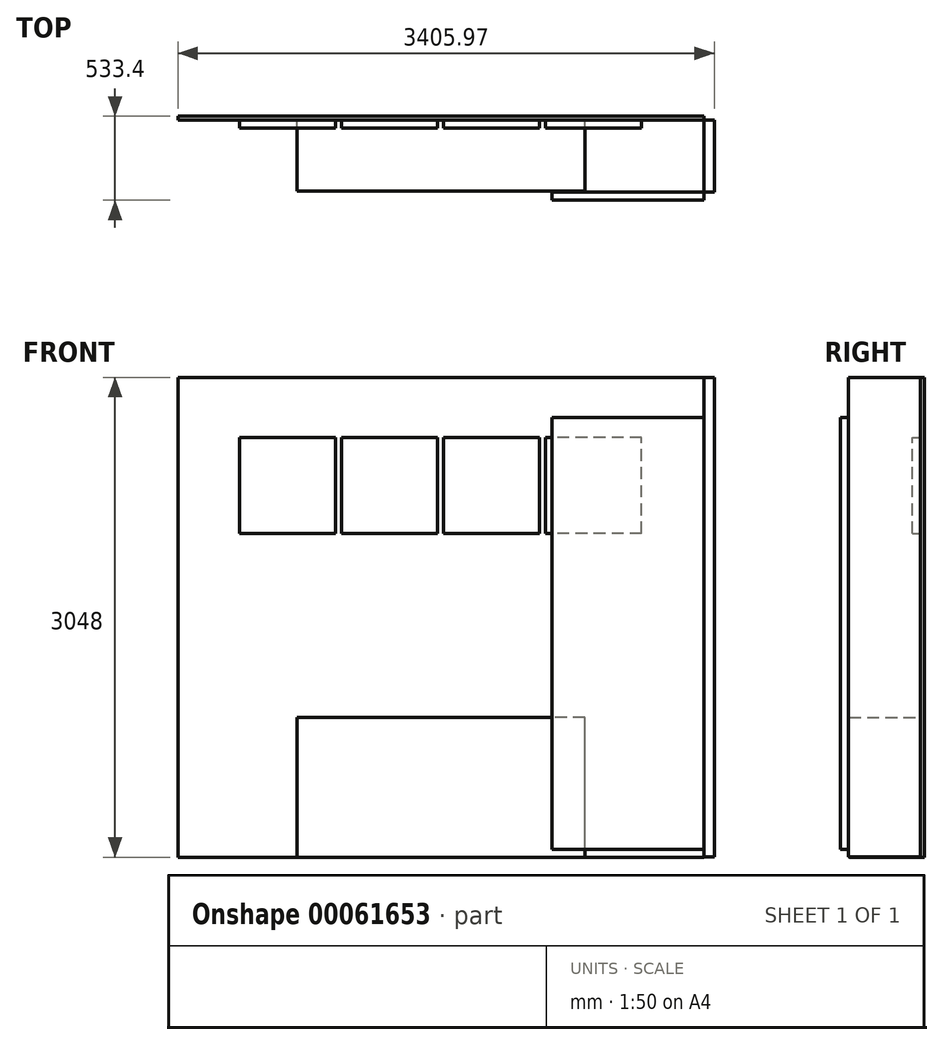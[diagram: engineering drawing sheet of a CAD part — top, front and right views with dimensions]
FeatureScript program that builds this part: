
annotation { "Feature Type Name" : "Feature", "Feature Type Description" : "" }
export const myFeature = defineFeature(function(context is Context, id is Id, definition is map)
    precondition{}
    {
        {
            var Q0;
            Q0=qCreatedBy(makeId("Front.planeOp"),FACE);
            var sketch = newSketch(context, id + "F0", { "sketchPlane" : qUnion([Q0])});
            skLineSegment(sketch, "E0.rect.bottom", {"start": v(1670.05, -1524) * mm, "end": v(-1670.05, -1524) * mm});
            skLineSegment(sketch, "E0.rect.top", {"start": v(1670.05, 1524) * mm, "end": v(-1670.05, 1524) * mm});
            skLineSegment(sketch, "E0.rect.left", {"start": v(1670.05, -1524) * mm, "end": v(1670.05, 1524) * mm});
            skLineSegment(sketch, "E0.rect.right", {"start": v(-1670.05, -1524) * mm, "end": v(-1670.05, 1524) * mm});
            skPoint(sketch, "E0.rect.middle", {"position": v(0, 0) * mm});
            skSolve(sketch);
        }
        {
            var Q0;
            Q0=makeQuery(id+"F0.imprint","IMPRINT",FACE,{"disambiguationData":[TD([[makeQuery(id+"F0.imprint","IMPRINT",EDGE,{"derivedFrom":sQuery(id+"F0.wireOp",EDGE,"E0.rect.bottom")}),-1.0]])]});
            extrude(context, id + "F1", {"entities" : qUnion([Q0]), "depth" : 25.4 * mm});
        }
        {
            var Q0;
            Q0=makeQuery(id+"F1.opExtrude","CAP_FACE",FACE,{"disambiguationData":[OSD([sQuery(id+"F0.wireOp",EDGE,"E0.rect.bottom"),sQuery(id+"F0.wireOp",EDGE,"E0.rect.top"),sQuery(id+"F0.wireOp",EDGE,"E0.rect.left"),sQuery(id+"F0.wireOp",EDGE,"E0.rect.right")])],"isStart":false});
            var sketch = newSketch(context, id + "F2", { "sketchPlane" : qUnion([Q0])});
            skLineSegment(sketch, "E1.rect.bottom", {"start": v(-668.38, 533.23) * mm, "end": v(-1277.98, 533.23) * mm});
            skLineSegment(sketch, "E1.rect.top", {"start": v(-668.38, 1142.83) * mm, "end": v(-1277.98, 1142.83) * mm});
            skLineSegment(sketch, "E1.rect.left", {"start": v(-668.38, 533.23) * mm, "end": v(-668.38, 1142.83) * mm});
            skLineSegment(sketch, "E1.rect.right", {"start": v(-1277.98, 533.23) * mm, "end": v(-1277.98, 1142.83) * mm});
            skPoint(sketch, "E1.rect.middle", {"position": v(-973.18, 838.03) * mm});
            skLineSegment(sketch, "E2.1.0.0", {"start": v(-20.68, 1142.83) * mm, "end": v(-630.28, 1142.83) * mm});
            skLineSegment(sketch, "E2.1.0.1", {"start": v(-20.68, 533.23) * mm, "end": v(-20.68, 1142.83) * mm});
            skLineSegment(sketch, "E2.1.0.2", {"start": v(-20.68, 533.23) * mm, "end": v(-630.28, 533.23) * mm});
            skLineSegment(sketch, "E2.1.0.3", {"start": v(-630.28, 533.23) * mm, "end": v(-630.28, 1142.83) * mm});
            skLineSegment(sketch, "E2.2.0.0", {"start": v(627.02, 1142.83) * mm, "end": v(17.42, 1142.83) * mm});
            skLineSegment(sketch, "E2.2.0.1", {"start": v(627.02, 533.23) * mm, "end": v(627.02, 1142.83) * mm});
            skLineSegment(sketch, "E2.2.0.2", {"start": v(627.02, 533.23) * mm, "end": v(17.42, 533.23) * mm});
            skLineSegment(sketch, "E2.2.0.3", {"start": v(17.42, 533.23) * mm, "end": v(17.42, 1142.83) * mm});
            skLineSegment(sketch, "E2.3.0.0", {"start": v(1274.72, 1142.83) * mm, "end": v(665.12, 1142.83) * mm});
            skLineSegment(sketch, "E2.3.0.1", {"start": v(1274.72, 533.23) * mm, "end": v(1274.72, 1142.83) * mm});
            skLineSegment(sketch, "E2.3.0.2", {"start": v(1274.72, 533.23) * mm, "end": v(665.12, 533.23) * mm});
            skLineSegment(sketch, "E2.3.0.3", {"start": v(665.12, 533.23) * mm, "end": v(665.12, 1142.83) * mm});
            skLineSegment(sketch, "E2.direction1", {"start": v(-1277.98, 1142.83) * mm, "end": v(-630.28, 1142.83) * mm, "construction": true});
            skLineSegment(sketch, "E3", {"start": v(0, 1524) * mm, "end": v(0, -1524) * mm, "construction": true});
            skLineSegment(sketch, "E4", {"start": v(1670.05, 1239.73) * mm, "end": v(704.85, 1239.73) * mm, "construction": true});
            skLineSegment(sketch, "E5.rect.bottom", {"start": v(914.4, -1538.16) * mm, "end": v(-914.4, -1538.16) * mm});
            skLineSegment(sketch, "E5.rect.top", {"start": v(914.4, -636.46) * mm, "end": v(-914.4, -636.46) * mm});
            skLineSegment(sketch, "E5.rect.left", {"start": v(914.4, -1538.16) * mm, "end": v(914.4, -636.46) * mm});
            skLineSegment(sketch, "E5.rect.right", {"start": v(-914.4, -1538.16) * mm, "end": v(-914.4, -636.46) * mm});
            skPoint(sketch, "E5.rect.middle", {"position": v(0, -1087.3) * mm});
            skLineSegment(sketch, "E6.bottom", {"start": v(1670.05, 1524) * mm, "end": v(1735.92, 1524) * mm});
            skLineSegment(sketch, "E6.top", {"start": v(1670.05, -1522.57) * mm, "end": v(1735.92, -1522.57) * mm});
            skLineSegment(sketch, "E6.left", {"start": v(1670.05, 1524) * mm, "end": v(1670.05, -1522.57) * mm});
            skLineSegment(sketch, "E6.right", {"start": v(1735.92, 1524) * mm, "end": v(1735.92, -1522.57) * mm});
            skLineSegment(sketch, "E7", {"start": v(704.85, 1239.73) * mm, "end": v(704.85, -1158.54) * mm, "construction": true});
            skLineSegment(sketch, "E8", {"start": v(704.85, -1158.54) * mm, "end": v(914.4, -1158.54) * mm, "construction": true});
            skSolve(sketch);
        }
        {
            var Q0;
            Q0=makeQuery(id+"F2.imprint","IMPRINT",FACE,{"disambiguationData":[TD([[makeQuery(id+"F2.imprint","IMPRINT",EDGE,{"derivedFrom":sQuery(id+"F2.wireOp",EDGE,"E1.rect.bottom")}),-1.0]])]});
            var Q1;
            Q1=makeQuery(id+"F2.imprint","IMPRINT",FACE,{"disambiguationData":[TD([[makeQuery(id+"F2.imprint","IMPRINT",EDGE,{"derivedFrom":sQuery(id+"F2.wireOp",EDGE,"E2.1.0.0")}),1.0]])]});
            var Q2;
            Q2=makeQuery(id+"F2.imprint","IMPRINT",FACE,{"disambiguationData":[TD([[makeQuery(id+"F2.imprint","IMPRINT",EDGE,{"derivedFrom":sQuery(id+"F2.wireOp",EDGE,"E2.2.0.0")}),1.0]])]});
            var Q3;
            Q3=makeQuery(id+"F2.imprint","IMPRINT",FACE,{"disambiguationData":[TD([[makeQuery(id+"F2.imprint","IMPRINT",EDGE,{"derivedFrom":sQuery(id+"F2.wireOp",EDGE,"E2.3.0.0")}),1.0]])]});
            extrude(context, id + "F3", {"entities" : qUnion([Q0, Q1, Q2, Q3]), "depth" : 50.8 * mm});
        }
        {
            var Q0;
            {var subQ0=sQuery(id+"F2.wireOp",EDGE,"E5.rect.top");Q0=makeQuery(id+"F2.imprint","IMPRINT",FACE,{"disambiguationData":[TD([[makeQuery(id+"F2.imprint","IMPRINT",EDGE,{"derivedFrom":subQ0}),1.0]])]});}
            extrude(context, id + "F4", {"entities" : qUnion([Q0]), "depth" : 450.85 * mm});
        }
        {
            var Q0;
            Q0=makeQuery(id+"F2.imprint","IMPRINT",FACE,{"disambiguationData":[TD([[makeQuery(id+"F2.imprint","IMPRINT",EDGE,{"derivedFrom":sQuery(id+"F2.wireOp",EDGE,"E6.bottom")}),-1.0]])]});
            extrude(context, id + "F5", {"entities" : qUnion([Q0]), "depth" : 457.2 * mm});
        }
        {
            var Q0;
            Q0=makeQuery(id+"F5.opExtrude","CAP_FACE",FACE,{"disambiguationData":[OSD([sQuery(id+"F2.wireOp",EDGE,"E6.bottom"),sQuery(id+"F2.wireOp",EDGE,"E6.top"),sQuery(id+"F2.wireOp",EDGE,"E6.left"),sQuery(id+"F2.wireOp",EDGE,"E6.right")])],"isStart":false});
            var sketch = newSketch(context, id + "F6", { "sketchPlane" : qUnion([Q0])});
            skLineSegment(sketch, "E9.bottom", {"start": v(1670.05, -1475.62) * mm, "end": v(704.85, -1475.62) * mm});
            skLineSegment(sketch, "E9.top", {"start": v(1670.05, 1267.58) * mm, "end": v(704.85, 1267.58) * mm});
            skLineSegment(sketch, "E9.left", {"start": v(1670.05, -1475.62) * mm, "end": v(1670.05, 1267.58) * mm});
            skLineSegment(sketch, "E9.right", {"start": v(704.85, -1475.62) * mm, "end": v(704.85, 1267.58) * mm});
            skSolve(sketch);
        }
        {
            var Q0;
            Q0=makeQuery(id+"F6.imprint","IMPRINT",FACE,{"disambiguationData":[TD([[makeQuery(id+"F6.imprint","IMPRINT",EDGE,{"derivedFrom":sQuery(id+"F6.wireOp",EDGE,"E9.bottom")}),-1.0]])]});
            extrude(context, id + "F7", {"entities" : qUnion([Q0]), "depth" : 50.8 * mm});
        }
    });
